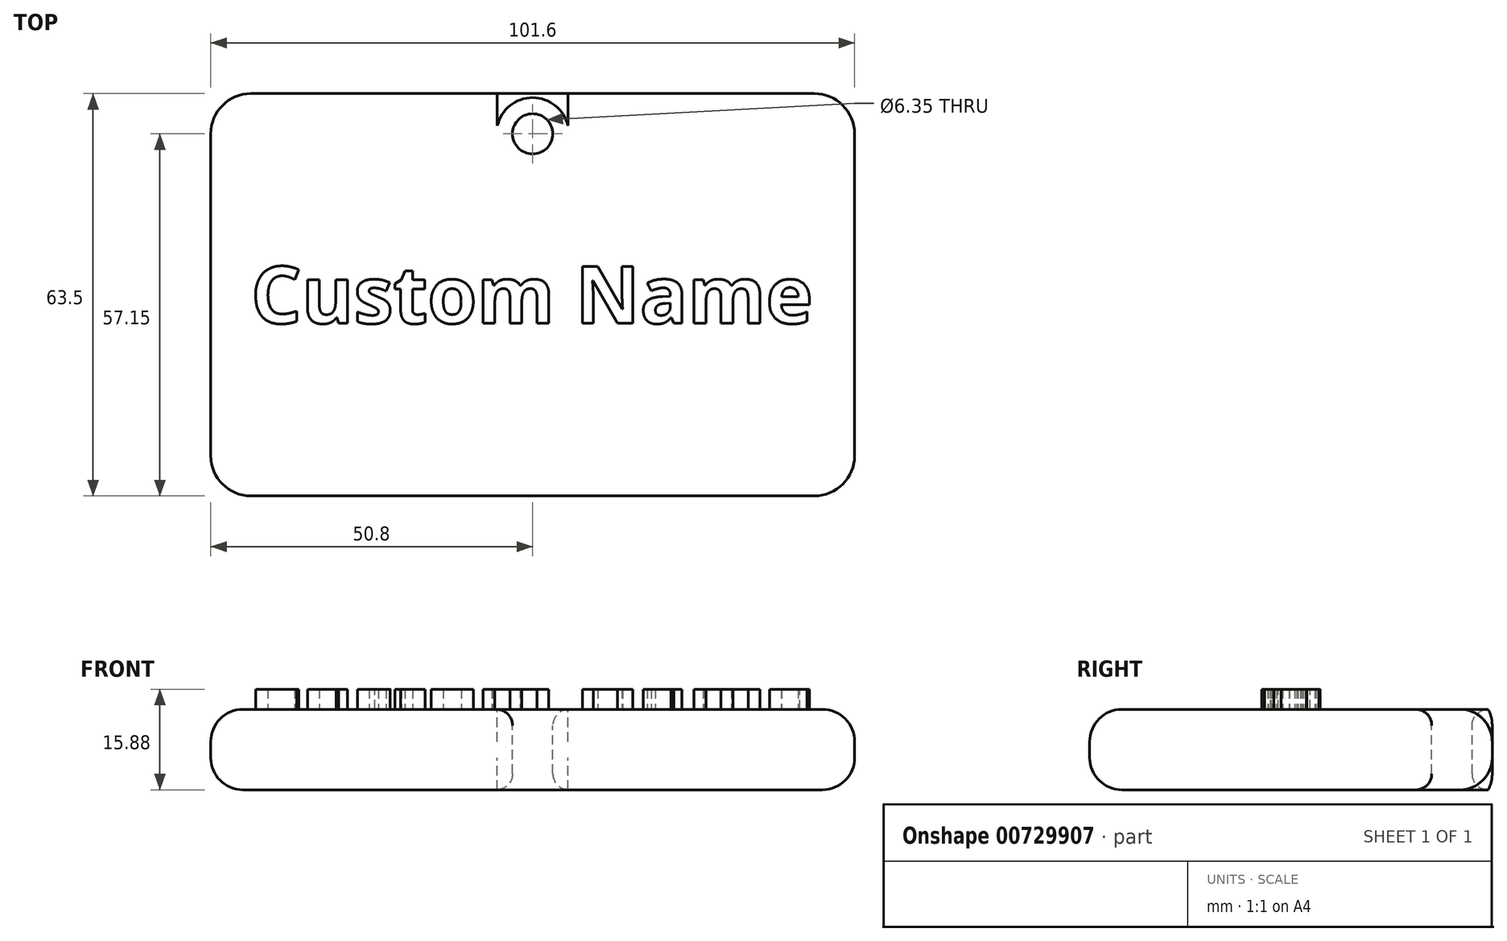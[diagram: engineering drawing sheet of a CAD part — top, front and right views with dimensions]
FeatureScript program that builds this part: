
annotation { "Feature Type Name" : "Feature", "Feature Type Description" : "" }
export const myFeature = defineFeature(function(context is Context, id is Id, definition is map)
    precondition{}
    {
        {
            var Q0;
            Q0=qCreatedBy(makeId("Top.planeOp"),FACE);
            var sketch = newSketch(context, id + "F0", { "sketchPlane" : qUnion([Q0])});
            skLineSegment(sketch, "E0.bottom", {"start": v(50.8, 31.75) * mm, "end": v(-50.8, 31.75) * mm});
            skLineSegment(sketch, "E0.top", {"start": v(50.8, -31.75) * mm, "end": v(-50.8, -31.75) * mm});
            skLineSegment(sketch, "E0.left", {"start": v(50.8, 31.75) * mm, "end": v(50.8, -31.75) * mm});
            skLineSegment(sketch, "E0.right", {"start": v(-50.8, 31.75) * mm, "end": v(-50.8, -31.75) * mm});
            skPoint(sketch, "E0.middle", {"position": v(0, 0) * mm});
            skSolve(sketch);
        }
        {
            var Q0;
            Q0 = qSketchRegion(id + "F0", true);
            extrude(context, id + "F1", {"entities" : qUnion([Q0]), "depth" : 12.7 * mm, "offsetDistance" : 25.4 * mm});
        }
        {
            var Q0;
            Q0=makeQuery(id+"F1.opExtrude","CAP_FACE",FACE,{"disambiguationData":[OSD([sQuery(id+"F0.wireOp",EDGE,"E0.bottom"),sQuery(id+"F0.wireOp",EDGE,"E0.top"),sQuery(id+"F0.wireOp",EDGE,"E0.left"),sQuery(id+"F0.wireOp",EDGE,"E0.right")])],"isStart":false});
            var sketch = newSketch(context, id + "F2", { "sketchPlane" : qUnion([Q0])});
            skText(sketch, "E1", { "text": "Custom Name", "fontName": "OpenSans-Bold.ttf"});
            const initialGuessF2  = {"E1": [-0.04445, -0.0045, 1, 0, 0.00902]};
            skSetInitialGuess(sketch, initialGuessF2);
            skSolve(sketch);
        }
        {
            var Q0;
            Q0 = qSketchRegion(id + "F2", true);
            extrude(context, id + "F3", {"entities" : qUnion([Q0]), "operationType" : NewBodyOperationType.ADD, "depth" : 3.17 * mm, "offsetDistance" : 25.4 * mm});
        }
        {
            var Q0;
            Q0=makeQuery(id+"F3.opExtrude","CAP_FACE",FACE,{"disambiguationData":[OSD([sQuery(id+"F2.wireOp",EDGE,"E1.sketch_text.stroke-15"),sQuery(id+"F2.wireOp",EDGE,"E1.sketch_text.stroke-16"),sQuery(id+"F2.wireOp",EDGE,"E1.sketch_text.stroke-17"),sQuery(id+"F2.wireOp",EDGE,"E1.sketch_text.stroke-18"),sQuery(id+"F2.wireOp",EDGE,"E1.sketch_text.stroke-19"),sQuery(id+"F2.wireOp",EDGE,"E1.sketch_text.stroke-20"),sQuery(id+"F2.wireOp",EDGE,"E1.sketch_text.stroke-21"),sQuery(id+"F2.wireOp",EDGE,"E1.sketch_text.stroke-22"),sQuery(id+"F2.wireOp",EDGE,"E1.sketch_text.stroke-23"),sQuery(id+"F2.wireOp",EDGE,"E1.sketch_text.stroke-24"),sQuery(id+"F2.wireOp",EDGE,"E1.sketch_text.stroke-25"),sQuery(id+"F2.wireOp",EDGE,"E1.sketch_text.stroke-26"),sQuery(id+"F2.wireOp",EDGE,"E1.sketch_text.stroke-27"),sQuery(id+"F2.wireOp",EDGE,"E1.sketch_text.stroke-28"),sQuery(id+"F2.wireOp",EDGE,"E1.sketch_text.stroke-29"),sQuery(id+"F2.wireOp",EDGE,"E1.sketch_text.stroke-30"),sQuery(id+"F2.wireOp",EDGE,"E1.sketch_text.stroke-31")])],"isStart":false});
            var sketch = newSketch(context, id + "F4", { "sketchPlane" : qUnion([Q0])});
            skCircle(sketch, "E2", {"center": v(0, 25.4) * mm, "radius": 3.18 * mm});
            skLineSegment(sketch, "E3", {"start": v(0, 25.4) * mm, "end": v(0, 31.75) * mm, "construction": true});
            skSolve(sketch);
        }
        {
            var Q0;
            Q0 = qSketchRegion(id + "F4", true);
            extrude(context, id + "F5", {"entities" : qUnion([Q0]), "operationType" : NewBodyOperationType.REMOVE, "oppositeDirection" : true, "depth" : 25.4 * mm, "offsetDistance" : 25.4 * mm});
        }
        {
            var Q0;
            {var subQ0=sQuery(id+"F0.wireOp",EDGE,"E0.top");var subQ1=sQuery(id+"F0.wireOp",EDGE,"E0.right");var subQ2=sQuery(id+"F0.wireOp",EDGE,"E0.bottom");var subQ3=sQuery(id+"F0.wireOp",EDGE,"E0.left");Q0=makeQuery(id+"F5.boolean.opBoolean","INTERSECT",EDGE,{"derivedFrom":[makeQuery(id+"F3.boolean.opBoolean","SPLIT",FACE,{"disambiguationData":[TD([makeQuery(id+"F1.opExtrude","SWEPT_FACE",FACE,{"disambiguationData":[OSD([subQ2])]})])],"derivedFrom":makeQuery(id+"F1.opExtrude","CAP_FACE",FACE,{"disambiguationData":[OSD([subQ2,subQ0,subQ3,subQ1])],"isStart":false})}),makeQuery(id+"F5.opExtrude","SWEPT_FACE",FACE,{"disambiguationData":[OSD([sQuery(id+"F4.wireOp",EDGE,"E2")])]})]});}
            var Q1;
            Q1=makeQuery(id+"F5.boolean.opBoolean","INTERSECT",EDGE,{"derivedFrom":[makeQuery(id+"F1.opExtrude","CAP_FACE",FACE,{"disambiguationData":[OSD([sQuery(id+"F0.wireOp",EDGE,"E0.bottom"),sQuery(id+"F0.wireOp",EDGE,"E0.top"),sQuery(id+"F0.wireOp",EDGE,"E0.left"),sQuery(id+"F0.wireOp",EDGE,"E0.right")])],"isStart":true}),makeQuery(id+"F5.opExtrude","SWEPT_FACE",FACE,{"disambiguationData":[OSD([sQuery(id+"F4.wireOp",EDGE,"E2")])]})]});
            fillet(context, id + "F6", {"entities" : qUnion([Q0, Q1]), "radius" : 2.54 * mm, "tangentPropagation" : true, "allowEdgeOverflow" : false});
        }
        {
            var Q0;
            Q0=makeQuery(id+"F1.opExtrude","SWEPT_EDGE",EDGE,{"disambiguationData":[OSD([sQuery(id+"F0.wireOp",EDGE,"E0.bottom"),sQuery(id+"F0.wireOp",EDGE,"E0.right")])]});
            var Q1;
            Q1=makeQuery(id+"F1.opExtrude","SWEPT_EDGE",EDGE,{"disambiguationData":[OSD([sQuery(id+"F0.wireOp",EDGE,"E0.top"),sQuery(id+"F0.wireOp",EDGE,"E0.right")])]});
            var Q2;
            Q2=makeQuery(id+"F1.opExtrude","SWEPT_EDGE",EDGE,{"disambiguationData":[OSD([sQuery(id+"F0.wireOp",EDGE,"E0.top"),sQuery(id+"F0.wireOp",EDGE,"E0.left")])]});
            var Q3;
            Q3=makeQuery(id+"F1.opExtrude","SWEPT_EDGE",EDGE,{"disambiguationData":[OSD([sQuery(id+"F0.wireOp",EDGE,"E0.bottom"),sQuery(id+"F0.wireOp",EDGE,"E0.left")])]});
            fillet(context, id + "F7", {"entities" : qUnion([Q0, Q1, Q2, Q3]), "radius" : 6.35 * mm, "tangentPropagation" : true, "allowEdgeOverflow" : false});
        }
        {
            var Q0;
            Q0=makeQuery(id+"F1.opExtrude","CAP_EDGE",EDGE,{"disambiguationData":[OSD([sQuery(id+"F0.wireOp",EDGE,"E0.bottom")])],"isStart":false});
            var Q1;
            {var subQ0=sQuery(id+"F0.wireOp",EDGE,"E0.top");var subQ1=sQuery(id+"F0.wireOp",EDGE,"E0.right");var subQ2=sQuery(id+"F0.wireOp",EDGE,"E0.bottom");var subQ3=sQuery(id+"F0.wireOp",EDGE,"E0.left");Q1=makeQuery(id+"F7.opFillet","BLEND_EDGE",EDGE,{"blendedFrom":[makeQuery(id+"F1.opExtrude","SWEPT_EDGE",EDGE,{"disambiguationData":[OSD([subQ2,subQ1])]}),makeQuery(id+"F3.boolean.opBoolean","SPLIT",FACE,{"disambiguationData":[TD([makeQuery(id+"F1.opExtrude","SWEPT_FACE",FACE,{"disambiguationData":[OSD([subQ2])]})])],"derivedFrom":makeQuery(id+"F1.opExtrude","CAP_FACE",FACE,{"disambiguationData":[OSD([subQ2,subQ0,subQ3,subQ1])],"isStart":false})})],"blendedInto":[makeQuery(id+"F3.boolean.opBoolean","SPLIT",FACE,{"disambiguationData":[TD([makeQuery(id+"F1.opExtrude","SWEPT_FACE",FACE,{"disambiguationData":[OSD([subQ2])]})])],"derivedFrom":makeQuery(id+"F1.opExtrude","CAP_FACE",FACE,{"disambiguationData":[OSD([subQ2,subQ0,subQ3,subQ1])],"isStart":false})})]});}
            var Q2;
            Q2=makeQuery(id+"F1.opExtrude","CAP_EDGE",EDGE,{"disambiguationData":[OSD([sQuery(id+"F0.wireOp",EDGE,"E0.top")])],"isStart":true});
            fillet(context, id + "F8", {"entities" : qUnion([Q0, Q1, Q2]), "radius" : 5.08 * mm, "tangentPropagation" : true, "allowEdgeOverflow" : false});
        }
    });
